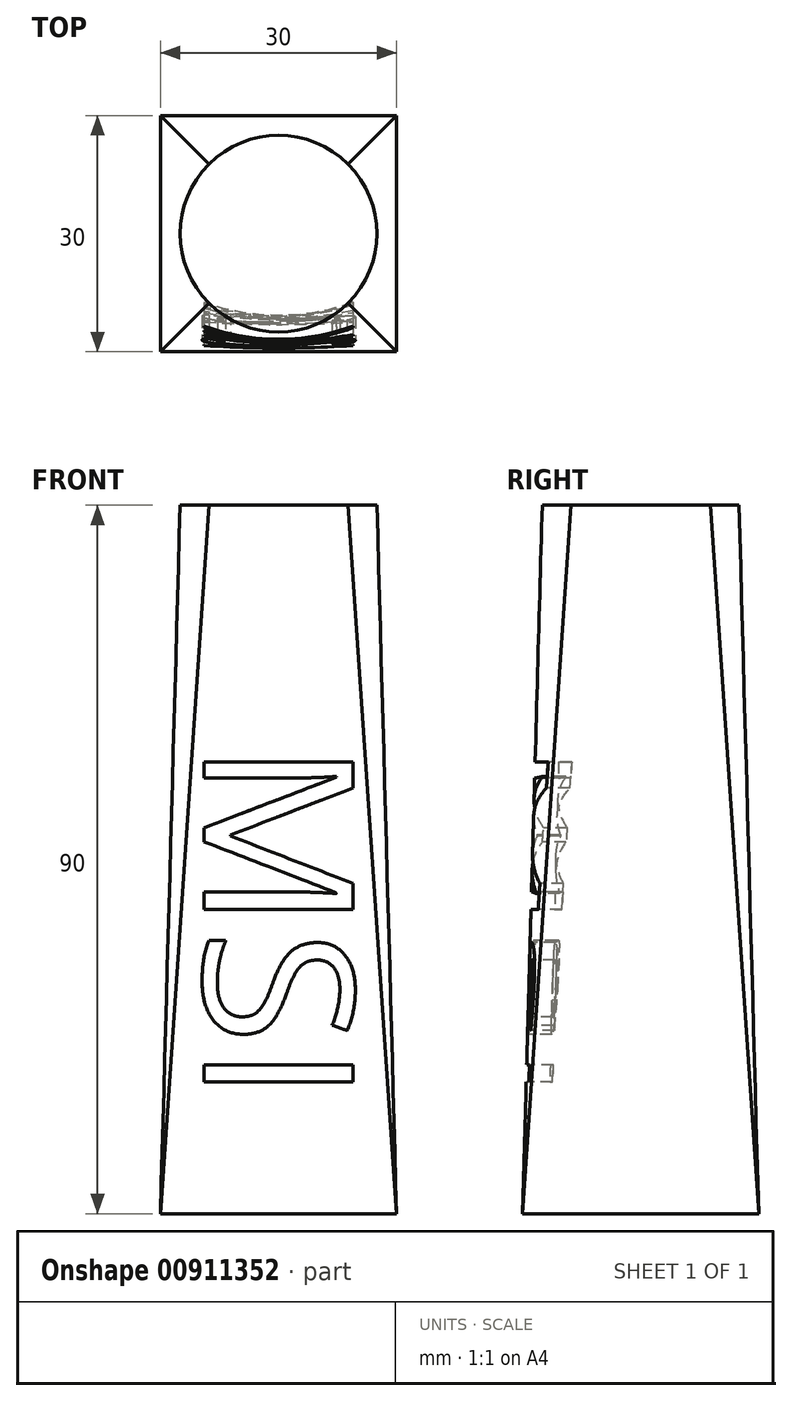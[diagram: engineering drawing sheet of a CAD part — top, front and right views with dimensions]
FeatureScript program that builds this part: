
annotation { "Feature Type Name" : "Feature", "Feature Type Description" : "" }
export const myFeature = defineFeature(function(context is Context, id is Id, definition is map)
    precondition{}
    {
        {
            var Q0;
            Q0=qCreatedBy(makeId("Top.planeOp"),FACE);
            var sketch = newSketch(context, id + "F0", { "sketchPlane" : qUnion([Q0])});
            skLineSegment(sketch, "E0.bottom", {"start": v(15, -15) * mm, "end": v(-15, -15) * mm});
            skLineSegment(sketch, "E0.top", {"start": v(15, 15) * mm, "end": v(-15, 15) * mm});
            skLineSegment(sketch, "E0.left", {"start": v(15, -15) * mm, "end": v(15, 15) * mm});
            skLineSegment(sketch, "E0.right", {"start": v(-15, -15) * mm, "end": v(-15, 15) * mm});
            skPoint(sketch, "E0.middle", {"position": v(0, 0) * mm});
            skSolve(sketch);
        }
        {
            var Q0;
            Q0=qCreatedBy(makeId("Top.planeOp"),FACE);
            cPlane(context, id + "F1", {"entities" : qUnion([Q0]), "cplaneType" : CPlaneType.OFFSET, "offset" : 90 * mm, "width" : 150 * mm, "height" : 150 * mm});
        }
        {
            var Q0;
            Q0=qCreatedBy(id+"F1.planeOp",FACE);
            var sketch = newSketch(context, id + "F2", { "sketchPlane" : qUnion([Q0])});
            skCircle(sketch, "E1", {"center": v(0, 0) * mm, "radius": 12.5 * mm});
            skSolve(sketch);
        }
        {
            var Q0;
            Q0=makeQuery(id+"F2.imprint","IMPRINT",FACE,{"disambiguationData":[TD([[makeQuery(id+"F2.imprint","IMPRINT",EDGE,{"derivedFrom":sQuery(id+"F2.wireOp",EDGE,"E1")}),1.0]])]});
            var Q1;
            Q1=makeQuery(id+"F0.imprint","IMPRINT",FACE,{"disambiguationData":[TD([[makeQuery(id+"F0.imprint","IMPRINT",EDGE,{"derivedFrom":sQuery(id+"F0.wireOp",EDGE,"E0.bottom")}),-1.0]])]});
            loft(context, id + "F3", {"sheetProfilesArray" : [{ "sheetProfileEntities" : qUnion([Q0]) }, { "sheetProfileEntities" : qUnion([Q1]) }]});
        }
        {
            var Q0;
            Q0=qCreatedBy(makeId("Front.planeOp"),FACE);
            cPlane(context, id + "F4", {"entities" : qUnion([Q0]), "cplaneType" : CPlaneType.OFFSET, "offset" : 75 * mm, "width" : 150 * mm, "height" : 150 * mm});
        }
        {
            var Q0;
            Q0=qCreatedBy(id+"F4.planeOp",FACE);
            var sketch = newSketch(context, id + "F5", { "sketchPlane" : qUnion([Q0])});
            skText(sketch, "E2", { "text": "MSI", "fontName": "OpenSans-Regular.ttf"});
            const initialGuessF5  = {"E2": [-0.00944, 0.06, 0, -1, 0.01909]};
            skSetInitialGuess(sketch, initialGuessF5);
            skSolve(sketch);
        }
        {
            var Q0;
            Q0 = qSketchRegion(id + "F5", true);
            var Q1;
            Q1=makeQuery(id+"F3.opLoft","SWEPT_BODY",BODY,{"disambiguationData":[OSD([makeQuery(id+"F0.imprint","IMPRINT",FACE,{"disambiguationData":[TD([[makeQuery(id+"F0.imprint","IMPRINT",EDGE,{"derivedFrom":sQuery(id+"F0.wireOp",EDGE,"E0.bottom")}),-1.0]])]}),makeQuery(id+"F2.imprint","IMPRINT",FACE,{"disambiguationData":[TD([[makeQuery(id+"F2.imprint","IMPRINT",EDGE,{"derivedFrom":sQuery(id+"F2.wireOp",EDGE,"E1")}),1.0]])]})])]});
            extrude(context, id + "F6", {"entities" : qUnion([Q0]), "operationType" : NewBodyOperationType.REMOVE, "endBound" : BoundingType.UP_TO_BODY, "oppositeDirection" : true, "depth" : 25 * mm, "endBoundEntityBody" : qUnion([Q1]), "hasOffset" : true, "offsetDistance" : 3 * mm, "offsetOppositeDirection" : true});
        }
    });
